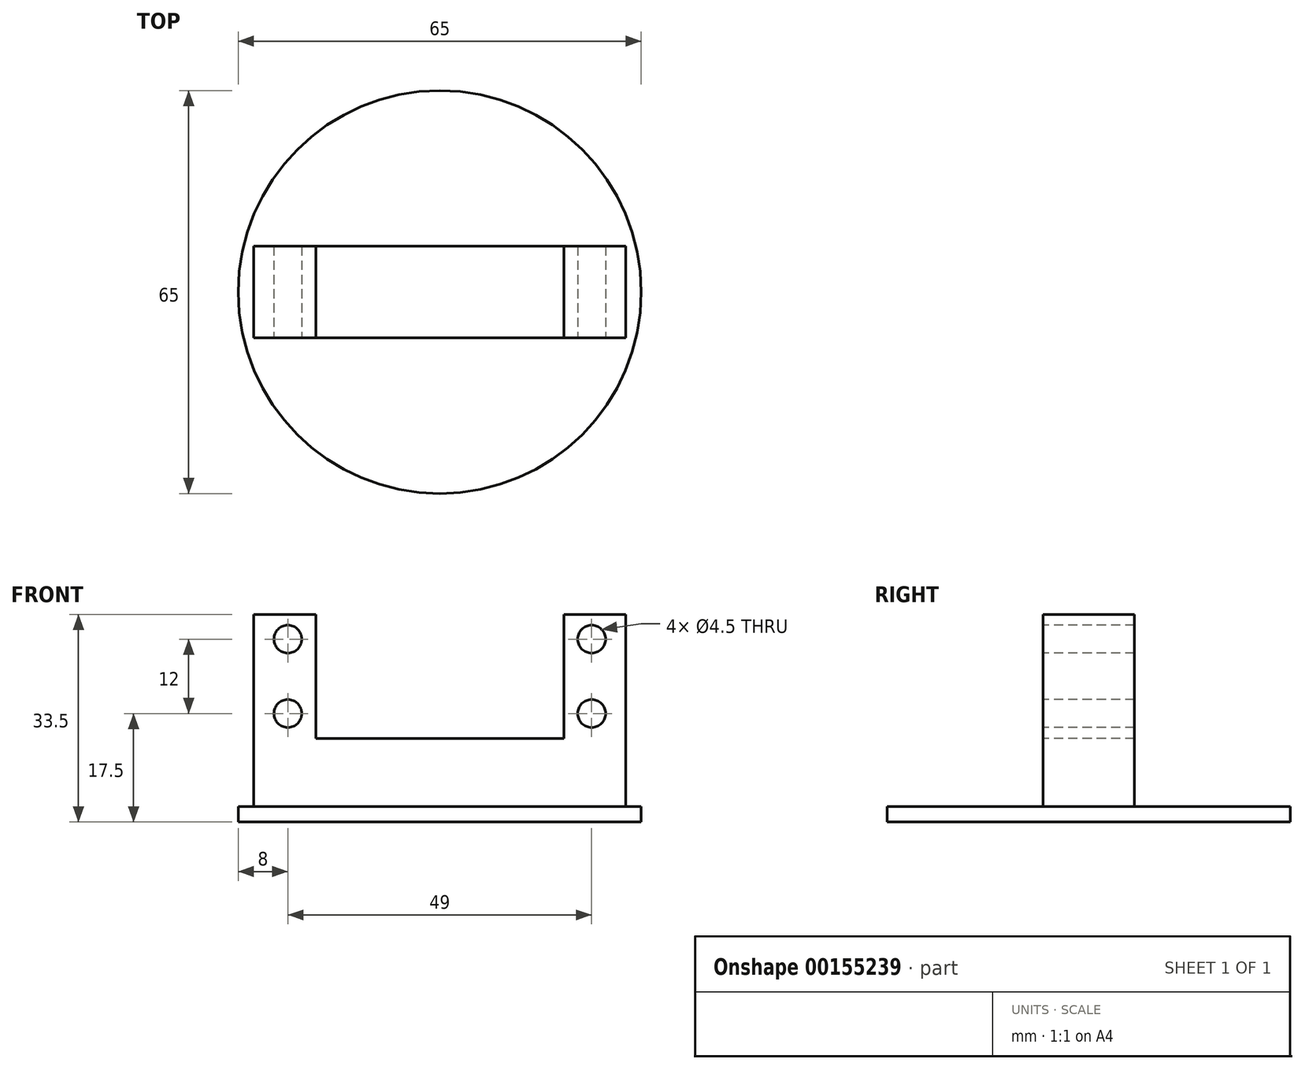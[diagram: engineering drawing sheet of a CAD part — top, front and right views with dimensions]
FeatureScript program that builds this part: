
annotation { "Feature Type Name" : "Feature", "Feature Type Description" : "" }
export const myFeature = defineFeature(function(context is Context, id is Id, definition is map)
    precondition{}
    {
        {
            var Q0;
            Q0=qCreatedBy(makeId("Top.planeOp"),FACE);
            var sketch = newSketch(context, id + "F0", { "sketchPlane" : qUnion([Q0])});
            skCircle(sketch, "E0", {"center": v(0, 0) * mm, "radius": 32.5 * mm});
            skSolve(sketch);
        }
        {
            var Q0;
            Q0 = qSketchRegion(id + "F0", true);
            extrude(context, id + "F1", {"entities" : qUnion([Q0]), "depth" : 2.5 * mm});
        }
        {
            var Q0;
            Q0=makeQuery(id+"F1.opExtrude","CAP_FACE",FACE,{"disambiguationData":[OSD([sQuery(id+"F0.wireOp",EDGE,"E0")])],"isStart":false});
            var sketch = newSketch(context, id + "F2", { "sketchPlane" : qUnion([Q0])});
            skLineSegment(sketch, "E1.bottom", {"start": v(30, 7.38) * mm, "end": v(-30, 7.38) * mm});
            skLineSegment(sketch, "E1.top", {"start": v(30, -7.38) * mm, "end": v(-30, -7.38) * mm});
            skLineSegment(sketch, "E1.left", {"start": v(30, 7.38) * mm, "end": v(30, -7.38) * mm});
            skLineSegment(sketch, "E1.right", {"start": v(-30, 7.38) * mm, "end": v(-30, -7.38) * mm});
            skLineSegment(sketch, "E2.bottom", {"start": v(30, 7.38) * mm, "end": v(20, 7.38) * mm});
            skLineSegment(sketch, "E2.top", {"start": v(30, -7.38) * mm, "end": v(20, -7.38) * mm});
            skLineSegment(sketch, "E2.right", {"start": v(20, 7.38) * mm, "end": v(20, -7.38) * mm});
            skLineSegment(sketch, "E3.bottom", {"start": v(-30, 7.38) * mm, "end": v(-20, 7.38) * mm});
            skLineSegment(sketch, "E3.top", {"start": v(-30, -7.38) * mm, "end": v(-20, -7.38) * mm});
            skLineSegment(sketch, "E3.right", {"start": v(-20, 7.38) * mm, "end": v(-20, -7.38) * mm});
            skSolve(sketch);
        }
        {
            var Q0;
            Q0 = qSketchRegion(id + "F2", true);
            extrude(context, id + "F3", {"entities" : qUnion([Q0]), "operationType" : NewBodyOperationType.ADD, "depth" : 11 * mm});
        }
        {
            var Q0;
            Q0=makeQuery(id+"F3.opExtrude","CAP_FACE",FACE,{"disambiguationData":[OSD([sQuery(id+"F2.wireOp",EDGE,"E1.bottom"),sQuery(id+"F2.wireOp",EDGE,"E1.top"),sQuery(id+"F2.wireOp",EDGE,"E2.bottom"),sQuery(id+"F2.wireOp",EDGE,"E2.top"),sQuery(id+"F2.wireOp",EDGE,"E1.left"),sQuery(id+"F2.wireOp",EDGE,"E3.bottom"),sQuery(id+"F2.wireOp",EDGE,"E3.top"),sQuery(id+"F2.wireOp",EDGE,"E1.right")])],"isStart":false});
            var sketch = newSketch(context, id + "F4", { "sketchPlane" : qUnion([Q0])});
            skLineSegment(sketch, "E4.bottom", {"start": v(30, 7.38) * mm, "end": v(20, 7.38) * mm});
            skLineSegment(sketch, "E4.top", {"start": v(30, -7.38) * mm, "end": v(20, -7.38) * mm});
            skLineSegment(sketch, "E4.left", {"start": v(30, 7.38) * mm, "end": v(30, -7.38) * mm});
            skLineSegment(sketch, "E4.right", {"start": v(20, 7.38) * mm, "end": v(20, -7.38) * mm});
            skLineSegment(sketch, "E5.bottom", {"start": v(-30, 7.38) * mm, "end": v(-20, 7.38) * mm});
            skLineSegment(sketch, "E5.top", {"start": v(-30, -7.38) * mm, "end": v(-20, -7.38) * mm});
            skLineSegment(sketch, "E5.left", {"start": v(-30, 7.38) * mm, "end": v(-30, -7.38) * mm});
            skLineSegment(sketch, "E5.right", {"start": v(-20, 7.38) * mm, "end": v(-20, -7.38) * mm});
            skSolve(sketch);
        }
        {
            var Q0;
            Q0 = qSketchRegion(id + "F4", true);
            extrude(context, id + "F5", {"entities" : qUnion([Q0]), "operationType" : NewBodyOperationType.ADD, "depth" : 20 * mm});
        }
        {
            var Q0;
            Q0=makeQuery(id+"F5.boolean.opBoolean","MERGE",FACE,{"derivedFrom":[makeQuery(id+"F3.opExtrude","SWEPT_FACE",FACE,{"disambiguationData":[OSD([sQuery(id+"F2.wireOp",EDGE,"E1.top"),sQuery(id+"F2.wireOp",EDGE,"E2.top"),sQuery(id+"F2.wireOp",EDGE,"E3.top")])]}),makeQuery(id+"F5.opExtrude","SWEPT_FACE",FACE,{"disambiguationData":[OSD([sQuery(id+"F4.wireOp",EDGE,"E4.top")])]}),makeQuery(id+"F5.opExtrude","SWEPT_FACE",FACE,{"disambiguationData":[OSD([sQuery(id+"F4.wireOp",EDGE,"E5.top")])]})]});
            var sketch = newSketch(context, id + "F6", { "sketchPlane" : qUnion([Q0])});
            skCircle(sketch, "E6", {"center": v(-24.5, 17.5) * mm, "radius": 2.25 * mm});
            skCircle(sketch, "E7", {"center": v(-24.5, 29.5) * mm, "radius": 2.25 * mm});
            skCircle(sketch, "E8", {"center": v(24.5, 17.5) * mm, "radius": 2.25 * mm});
            skCircle(sketch, "E9", {"center": v(24.5, 29.5) * mm, "radius": 2.25 * mm});
            skSolve(sketch);
        }
        {
            var Q0;
            Q0 = qSketchRegion(id + "F6", true);
            extrude(context, id + "F7", {"entities" : qUnion([Q0]), "operationType" : NewBodyOperationType.REMOVE, "oppositeDirection" : true, "depth" : 25.4 * mm});
        }
    });
